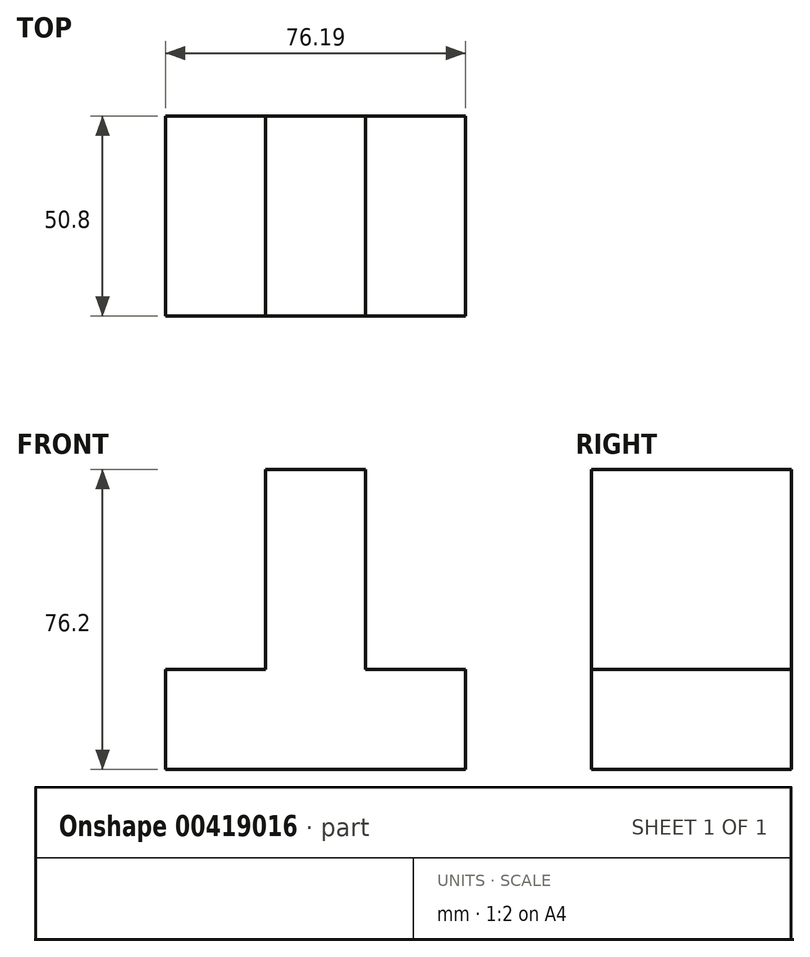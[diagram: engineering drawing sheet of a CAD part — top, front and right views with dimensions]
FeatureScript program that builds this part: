
annotation { "Feature Type Name" : "Feature", "Feature Type Description" : "" }
export const myFeature = defineFeature(function(context is Context, id is Id, definition is map)
    precondition{}
    {
        {
            var Q0;
            Q0=qCreatedBy(makeId("Front.planeOp"),FACE);
            var sketch = newSketch(context, id + "F0", { "sketchPlane" : qUnion([Q0])});
            skLineSegment(sketch, "E0", {"start": v(0, 0) * mm, "end": v(-76.2, 0) * mm});
            skLineSegment(sketch, "E1", {"start": v(-76.2, 0) * mm, "end": v(-76.2, 25.4) * mm});
            skLineSegment(sketch, "E2", {"start": v(-76.2, 25.4) * mm, "end": v(-50.8, 25.4) * mm});
            skLineSegment(sketch, "E3", {"start": v(-50.8, 25.4) * mm, "end": v(-50.8, 76.2) * mm});
            skLineSegment(sketch, "E4", {"start": v(0, 0) * mm, "end": v(0, 25.4) * mm});
            skLineSegment(sketch, "E5", {"start": v(0, 25.4) * mm, "end": v(-25.4, 25.4) * mm});
            skLineSegment(sketch, "E6", {"start": v(-25.4, 25.4) * mm, "end": v(-25.4, 76.2) * mm});
            skLineSegment(sketch, "E7", {"start": v(-50.8, 76.2) * mm, "end": v(-25.4, 76.2) * mm});
            skSolve(sketch);
        }
        {
            var Q0;
            Q0=makeQuery(id+"F0.imprint","IMPRINT",FACE,{"disambiguationData":[TD([[makeQuery(id+"F0.imprint","IMPRINT",EDGE,{"derivedFrom":sQuery(id+"F0.wireOp",EDGE,"E0")}),-1.0]])]});
            extrude(context, id + "F1", {"entities" : qUnion([Q0]), "depth" : 50.8 * mm});
        }
    });
